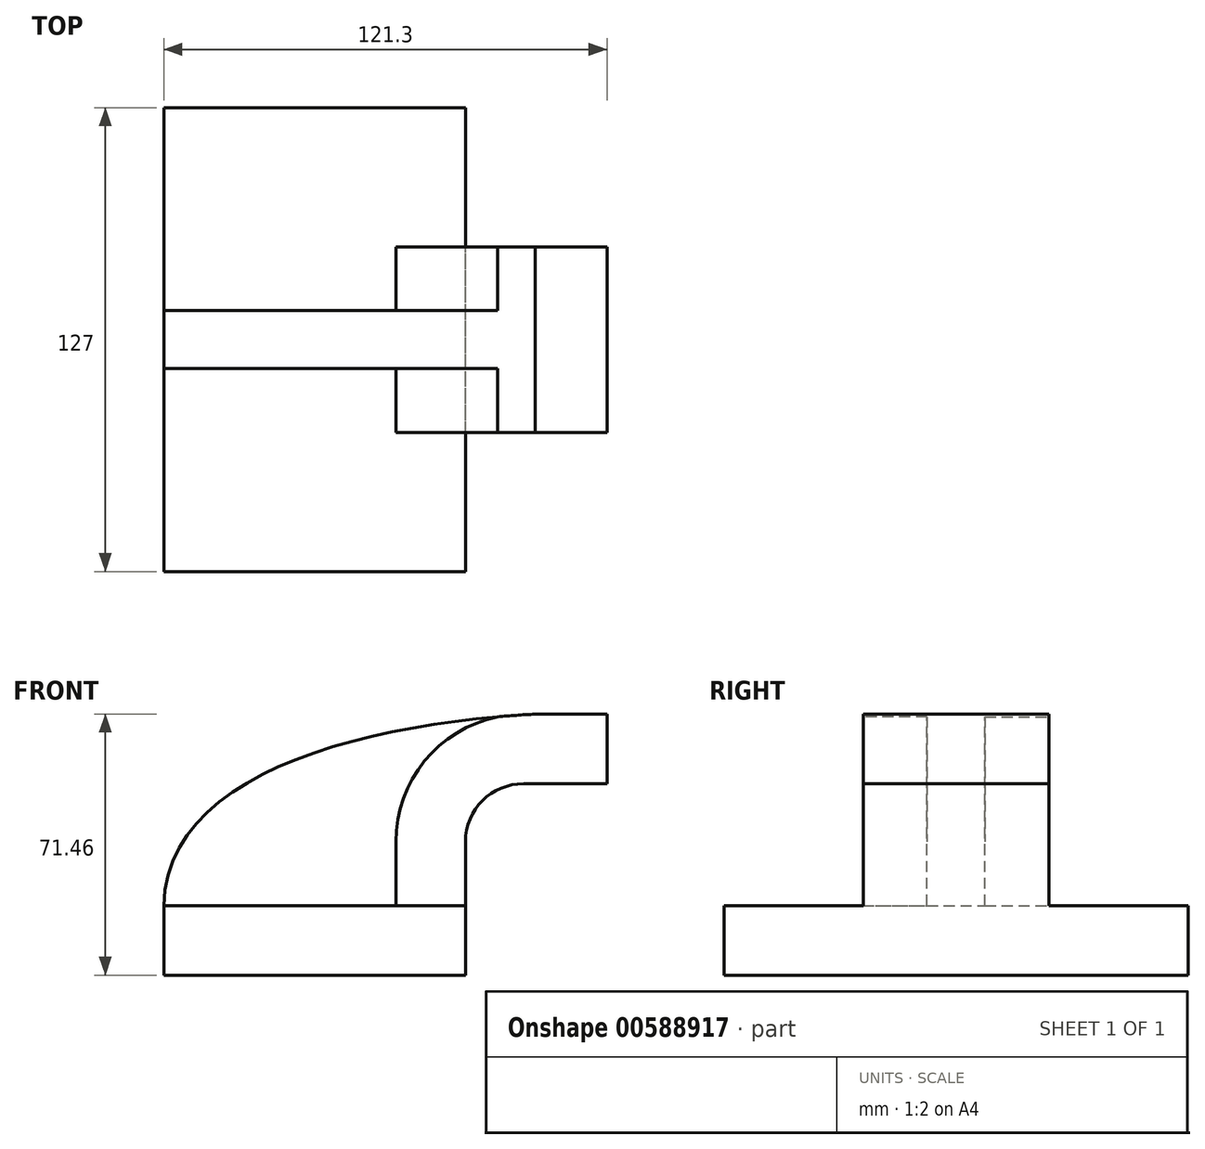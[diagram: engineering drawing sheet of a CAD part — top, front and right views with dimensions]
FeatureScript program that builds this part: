
annotation { "Feature Type Name" : "Feature", "Feature Type Description" : "" }
export const myFeature = defineFeature(function(context is Context, id is Id, definition is map)
    precondition{}
    {
        {
            var Q0;
            Q0=qCreatedBy(makeId("Front.planeOp"),FACE);
            var sketch = newSketch(context, id + "F0", { "sketchPlane" : qUnion([Q0])});
            skLineSegment(sketch, "E0.bottom", {"start": v(-41.28, -9.53) * mm, "end": v(41.28, -9.53) * mm});
            skLineSegment(sketch, "E0.top", {"start": v(-41.28, 9.53) * mm, "end": v(41.28, 9.53) * mm});
            skLineSegment(sketch, "E0.left", {"start": v(-41.28, -9.53) * mm, "end": v(-41.28, 9.53) * mm});
            skLineSegment(sketch, "E0.right", {"start": v(41.28, -9.53) * mm, "end": v(41.28, 9.53) * mm});
            skPoint(sketch, "E0.middle", {"position": v(0, 0) * mm});
            skLineSegment(sketch, "E1.bottom", {"start": v(60.32, 38.1) * mm, "end": v(111.12, 38.1) * mm});
            skLineSegment(sketch, "E1.top", {"start": v(60.32, 66.67) * mm, "end": v(111.12, 66.67) * mm});
            skLineSegment(sketch, "E1.left", {"start": v(60.33, 38.1) * mm, "end": v(60.32, 66.67) * mm});
            skLineSegment(sketch, "E1.right", {"start": v(111.12, 38.1) * mm, "end": v(111.12, 66.67) * mm});
            skPoint(sketch, "E1.middle", {"position": v(85.72, 52.39) * mm});
            skLineSegment(sketch, "E2", {"start": v(41.28, 9.53) * mm, "end": v(41.28, 27) * mm});
            skArc(sketch, "E3", {"start": v(41.27, 27) * mm, "mid": v(45.92, 38.23) * mm, "end": v(57.15, 42.88) * mm});
            skLineSegment(sketch, "E4", {"start": v(57.15, 42.88) * mm, "end": v(80.02, 42.88) * mm});
            skLineSegment(sketch, "E5.0", {"start": v(57.15, 61.93) * mm, "end": v(80.02, 61.93) * mm});
            skArc(sketch, "E5.1", {"start": v(22.22, 27) * mm, "mid": v(32.45, 51.7) * mm, "end": v(57.15, 61.93) * mm});
            skLineSegment(sketch, "E5.2", {"start": v(22.22, 9.53) * mm, "end": v(22.22, 27) * mm});
            skLineSegment(sketch, "E6", {"start": v(80.02, 42.88) * mm, "end": v(80.02, 61.93) * mm});
            skPoint(sketch, "E7.1.internal.snap0", {"position": v(60.32, 52.39) * mm});
            skFitSpline(sketch, "E7", {"points": [v(-41.28, 9.53) * mm, v(60.32, 61.93) * mm], "startDerivative": vector(1.77, 108.45) * mm, "endDerivative": vector(141.97, 7.76) * mm});
            skSolve(sketch);
        }
        {
            var Q0;
            Q0=makeQuery(id+"F0.imprint","IMPRINT",FACE,{"disambiguationData":[TD([[makeQuery(id+"F0.imprint","IMPRINT",EDGE,{"derivedFrom":sQuery(id+"F0.wireOp",EDGE,"E0.bottom")}),1.0]])]});
            extrude(context, id + "F1", {"entities" : qUnion([Q0]), "endBound" : BoundingType.SYMMETRIC, "depth" : 127 * mm, "offsetDistance" : 25.4 * mm});
        }
        {
            var Q0;
            {var subQ0=sQuery(id+"F0.wireOp",EDGE,"E2");Q0=makeQuery(id+"F0.imprint","IMPRINT",FACE,{"disambiguationData":[TD([[makeQuery(id+"F0.imprint","IMPRINT",EDGE,{"derivedFrom":subQ0}),1.0]])]});}
            extrude(context, id + "F2", {"entities" : qUnion([Q0]), "operationType" : NewBodyOperationType.ADD, "endBound" : BoundingType.SYMMETRIC, "depth" : 50.8 * mm, "offsetDistance" : 25.4 * mm});
        }
        {
            var Q0;
            {var subQ5=sQuery(id+"F0.wireOp",EDGE,"E6");Q0=makeQuery(id+"F0.imprint","IMPRINT",FACE,{"disambiguationData":[TD([[makeQuery(id+"F0.imprint","IMPRINT",EDGE,{"derivedFrom":subQ5}),1.0]])]});}
            extrude(context, id + "F3", {"entities" : qUnion([Q0]), "operationType" : NewBodyOperationType.ADD, "endBound" : BoundingType.SYMMETRIC, "depth" : 50.8 * mm, "offsetDistance" : 25.4 * mm});
        }
        {
            var Q0;
            {var subQ3=sQuery(id+"F0.wireOp",EDGE,"E5.2");Q0=makeQuery(id+"F0.imprint","IMPRINT",FACE,{"disambiguationData":[TD([[makeQuery(id+"F0.imprint","IMPRINT",EDGE,{"derivedFrom":subQ3}),1.0]])]});}
            extrude(context, id + "F4", {"entities" : qUnion([Q0]), "operationType" : NewBodyOperationType.ADD, "endBound" : BoundingType.SYMMETRIC, "depth" : 15.88 * mm, "offsetDistance" : 25.4 * mm});
        }
    });
